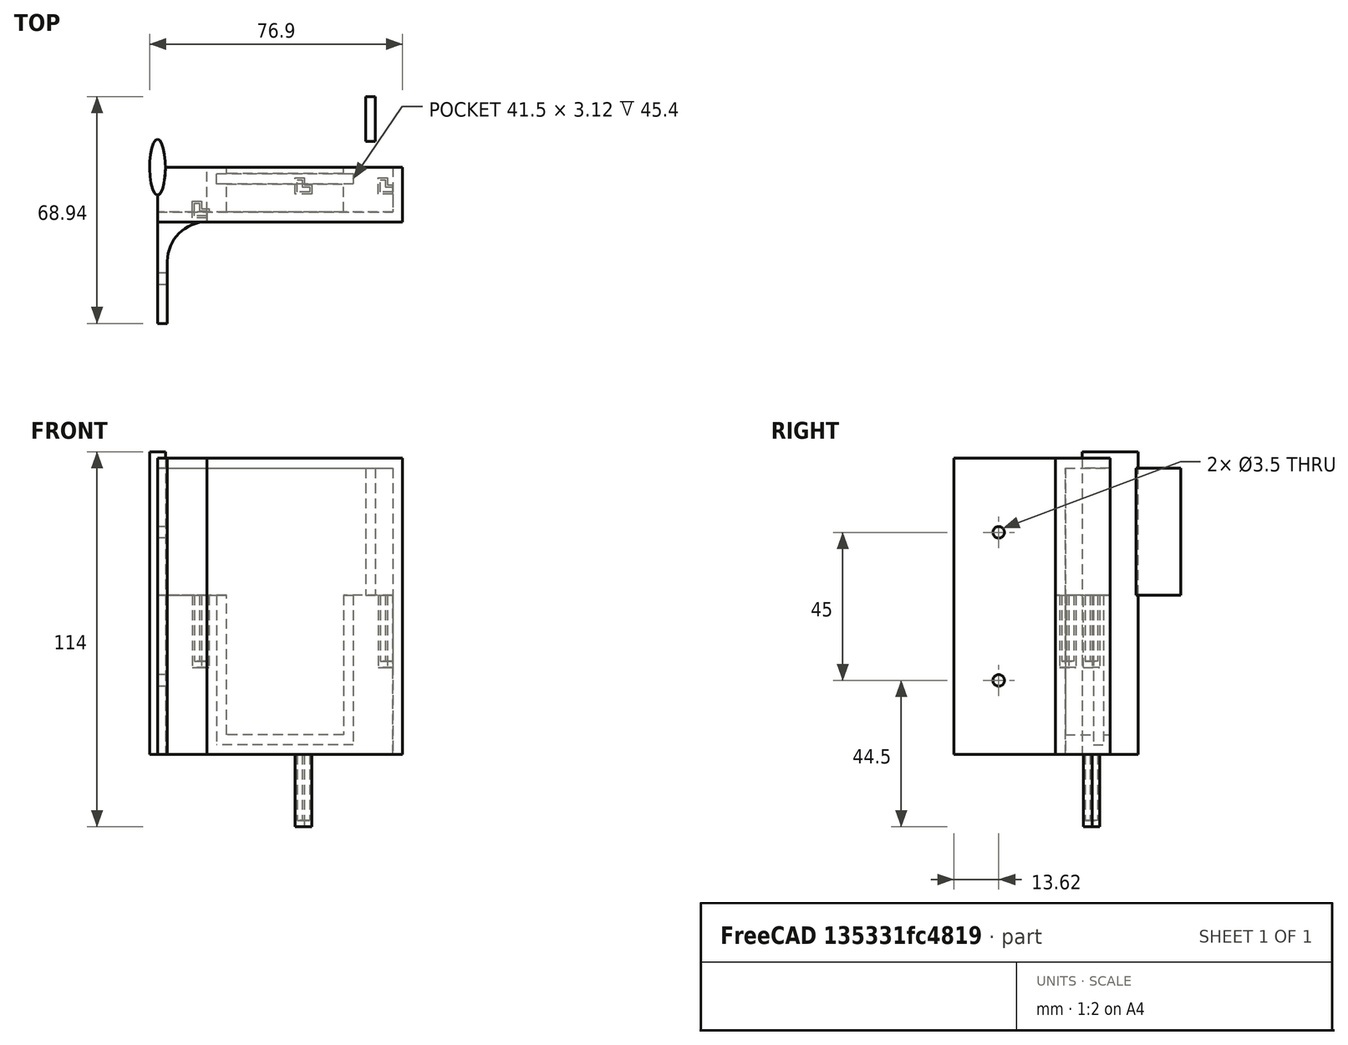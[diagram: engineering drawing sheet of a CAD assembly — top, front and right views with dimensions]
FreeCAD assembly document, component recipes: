
FREECAD ASSEMBLY — COMPONENT RECIPES ("rfid_mk2")

This assembly document has 9 components, labeled P0..P8 below (a component is one placed body or linked part). 8 of them carry a construction recipe — the FreeCAD feature program that regenerates the part from scratch, quoted from this document or its linked companion documents; the rest are supplied as boundary geometry only. No exploded tour is included for this assembly.
COMPONENT P0 — recipe-attached ("Holder", modeled in this document).
Construction recipe (the document's own serialized feature program — sketch geometry with constraints, then the solid features built on it; lengths are millimeters unless a unit is written):

FEATURE [Sketcher::SketchObject] Sketch  label="Holder Sketch"
  FullyConstrained = false
  MapMode = 5
  Support = -> [XY_Plane]
  expr: Constraints[8] = <<Holder Data>>.width
  expr: Constraints[9] = <<Holder Data>>.thick
  sketch-geometry (4):
    g0: LineSegment StartX=-28.25 StartY=6.81 StartZ=0 EndX=28.25 EndY=6.81 EndZ=0
    g1: LineSegment StartX=28.25 StartY=6.81 StartZ=0 EndX=28.25 EndY=-6.81 EndZ=0
    g2: LineSegment StartX=28.25 StartY=-6.81 StartZ=0 EndX=-28.25 EndY=-6.81 EndZ=0
    g3: LineSegment StartX=-28.25 StartY=-6.81 StartZ=0 EndX=-28.25 EndY=6.81 EndZ=0
  constraints (10):
    c: Coincident(g0,g1)
    c: Coincident(g1,g2)
    c: Coincident(g2,g3)
    c: Coincident(g3,g0)
    c: Horizontal(g2)
    c: Vertical(g3)
    c: Symmetric(g0,g0,g-2)
    c: Symmetric(g1,g0,g-1)
    c: DistanceX(g0,g0) = 56.5
    c: DistanceY(g1,g0) = 13.62
FEATURE [PartDesign::Pad] Pad  label="Holder Pad"
  AllowMultiFace = false
  Direction = (1,1,1)
  Length = 48.4
  Length2 = 100
  Profile = -> Sketch
  Type = 0
  expr: Length = <<Holder Data>>.height
FEATURE [Sketcher::SketchObject] Sketch001  label="RFID Slot"
  FullyConstrained = false
  MapMode = 5
  Placement = pos=(0,0,48.4) rot=(0,0,1;0rad)
  Support = -> [Pad]
  expr: Constraints[11] = <<Holder Data>>.thick / 2 - <<Holder Data>>.glass_clearance
  expr: Constraints[2] = <<Holder Data>>.rfid_gap
  expr: Constraints[10] = -<<Holder Data>>.width / 2 + <<General Data>>.wall
  expr: Constraints[1] = <<Holder Data>>.slot
  sketch-geometry (4):
    g0: LineSegment StartX=-25.25 StartY=4.81 StartZ=0 EndX=16.25 EndY=4.81 EndZ=0
    g1: LineSegment StartX=16.25 StartY=4.81 StartZ=0 EndX=16.25 EndY=1.69 EndZ=0
    g2: LineSegment StartX=16.25 StartY=1.69 StartZ=0 EndX=-25.25 EndY=1.69 EndZ=0
    g3: LineSegment StartX=-25.25 StartY=1.69 StartZ=0 EndX=-25.25 EndY=4.81 EndZ=0
  constraints (12):
    c: Vertical(g1)
    c: DistanceY(g1,g1) = 3.12
    c: DistanceX(g0,g0) = 41.5
    c: Coincident(g3,g0)
    c: Coincident(g1,g0)
    c: Coincident(g2,g1)
    c: Horizontal(g0)
    c: Horizontal(g2)
    c: Vertical(g3)
    c: Coincident(g2,g3)
    c: DistanceX(g-1,g2) = -25.25
    c: DistanceY(g-1,g0) = 4.81
FEATURE [PartDesign::Pocket] Pocket  label="RFID Slot Pocket"
  AllowMultiFace = false
  BaseFeature = -> Pad
  Length = 45.4
  Length2 = 100
  Profile = -> Sketch001
  Type = 0
  expr: Length = <<Holder Data>>.height - <<General Data>>.wall
FEATURE [Sketcher::SketchObject] Sketch002  label="Through Holder"
  FullyConstrained = false
  MapMode = 5
  Placement = pos=(0,-6.81,0) rot=(1,0,0;1.5708rad)
  Support = -> [Pocket]
  expr: Constraints[7] = <<General Data>>.wall * 2
  expr: Constraints[8] = <<Holder Data>>.height
  expr: Constraints[9] = <<Holder Data>>.width / 2 - <<General Data>>.wall * 2
  expr: Constraints[10] = <<Holder Data>>.rfid_gap - <<General Data>>.wall * 2
  sketch-geometry (4):
    g0: LineSegment StartX=-22.25 StartY=48.4 StartZ=0 EndX=13.25 EndY=48.4 EndZ=0
    g1: LineSegment StartX=13.25 StartY=48.4 StartZ=0 EndX=13.25 EndY=6 EndZ=0
    g2: LineSegment StartX=13.25 StartY=6 StartZ=0 EndX=-22.25 EndY=6 EndZ=0
    g3: LineSegment StartX=-22.25 StartY=6 StartZ=0 EndX=-22.25 EndY=48.4 EndZ=0
  constraints (11):
    c: Coincident(g0,g1)
    c: Coincident(g1,g2)
    c: Coincident(g2,g3)
    c: Coincident(g3,g0)
    c: Horizontal(g0)
    c: Vertical(g1)
    c: Vertical(g3)
    c: DistanceY(g-1,g2) = 6
    c: DistanceY(g-1,g0) = 48.4
    c: DistanceX(g2,g-1) = 22.25
    c: DistanceX(g2,g2) = 35.5
FEATURE [PartDesign::Pocket] Pocket001  label="Through Holder Pocket"
  AllowMultiFace = false
  BaseFeature = -> Pocket
  Length = 56.5
  Length2 = 100
  Profile = -> Sketch002
  Type = 0
  expr: Length = <<Holder Data>>.width
FEATURE [PartDesign::Body] Body  label="Holder"
  Group = -> [Sketch,Pad,Sketch001,Pocket,Sketch002,Pocket001]
  Origin = -> Origin
  Tip = -> Pocket001
COMPONENT P1 — recipe-attached ("Bracket Base", modeled in this document).
Construction recipe (the document's own serialized feature program — sketch geometry with constraints, then the solid features built on it; lengths are millimeters unless a unit is written):

FEATURE [Sketcher::SketchObject] Sketch003  label="Bracket Sketch"
  FullyConstrained = false
  MapMode = 5
  Support = -> [XY_Plane001]
  expr: Constraints[13] = <<Bracket Data>>.depth
  expr: Constraints[14] = <<General Data>>.wall
  expr: Constraints[15] = <<Bracket Data>>.width
  expr: Constraints[16] = <<Holder Data>>.thick + <<General Data>>.wall
  expr: Constraints[18] = <<Holder Data>>.thick / 2
  expr: Constraints[19] = <<Holder Data>>.width / 2
  expr: Constraints[17] = <<Bracket Data>>.width - <<General Data>>.wall - 0.01
  sketch-geometry (7):
    g0: LineSegment StartX=-43.25 StartY=6.81 StartZ=0 EndX=-43.25 EndY=-40.69 EndZ=0
    g1: LineSegment StartX=-43.25 StartY=-40.69 StartZ=0 EndX=-40.25 EndY=-40.69 EndZ=0
    g2: LineSegment StartX=-40.25 StartY=-40.69 StartZ=0 EndX=-40.25 EndY=-21.8 EndZ=0
    g3: LineSegment StartX=-28.26 StartY=-9.81 StartZ=0 EndX=-28.25 EndY=-9.81 EndZ=0
    g4: LineSegment StartX=-28.25 StartY=-9.81 StartZ=0 EndX=-28.25 EndY=6.81 EndZ=0
    g5: LineSegment StartX=-28.25 StartY=6.81 StartZ=0 EndX=-43.25 EndY=6.81 EndZ=0
    g6: ArcOfCircle CenterX=-28.26 CenterY=-21.8 CenterZ=0 NormalX=0 NormalY=0 NormalZ=1 AngleXU=0 Radius=11.99 StartAngle=1.5708 EndAngle=3.14159
  constraints (20):
    c: Vertical(g0)
    c: Coincident(g0,g1)
    c: Coincident(g1,g2)
    c: Vertical(g2)
    c: Horizontal(g3)
    c: Coincident(g3,g4)
    c: Vertical(g4)
    c: Coincident(g4,g5)
    c: Coincident(g5,g0)
    c: Horizontal(g5)
    c: Horizontal(g1)
    c: Tangent(g2,g6) = 1.5708
    c: Tangent(g3,g6) = 1.5708
    c: DistanceY(g0,g0) = 47.5
    c: DistanceX(g1,g1) = 3
    c: DistanceX(g5,g5) = 15
    c: DistanceY(g4,g4) = 16.62
    c: Radius(g6) = 11.99
    c: DistanceY(g-1,g4) = 6.81
    c: DistanceX(g4,g-1) = 28.25
FEATURE [PartDesign::Pad] Pad001  label="Bracket Pad"
  AllowMultiFace = false
  Direction = (1,1,1)
  Length = 90
  Length2 = 100
  Profile = -> Sketch003
  Type = 0
  expr: Length = <<General Data>>.height
FEATURE [Sketcher::SketchObject] Sketch004  label="Bracket Block Cutout Sketch"
  FullyConstrained = false
  MapMode = 5
  Placement = pos=(0,0,90) rot=(0,0,1;0rad)
  Support = -> [Pad001]
  expr: Constraints[8] = <<Holder Data>>.thick + <<General Data>>.wall
  expr: Constraints[9] = <<Bracket Data>>.width
  expr: Constraints[10] = <<Holder Data>>.thick / 2
  expr: Constraints[11] = <<Holder Data>>.width / 2
  sketch-geometry (4):
    g0: LineSegment StartX=-43.25 StartY=6.81 StartZ=0 EndX=-28.25 EndY=6.81 EndZ=0
    g1: LineSegment StartX=-28.25 StartY=6.81 StartZ=0 EndX=-28.25 EndY=-9.81 EndZ=0
    g2: LineSegment StartX=-28.25 StartY=-9.81 StartZ=0 EndX=-43.25 EndY=-9.81 EndZ=0
    g3: LineSegment StartX=-43.25 StartY=-9.81 StartZ=0 EndX=-43.25 EndY=6.81 EndZ=0
  constraints (12):
    c: Coincident(g0,g1)
    c: Coincident(g1,g2)
    c: Coincident(g2,g3)
    c: Coincident(g3,g0)
    c: Horizontal(g0)
    c: Horizontal(g2)
    c: Vertical(g1)
    c: Vertical(g3)
    c: DistanceY(g1,g1) = 16.62
    c: DistanceX(g0,g0) = 15
    c: DistanceY(g-1,g0) = 6.81
    c: DistanceX(g0,g-1) = 28.25
FEATURE [PartDesign::Pocket] Pocket002  label="Bracket Block Cutout"
  AllowMultiFace = false
  BaseFeature = -> Pad001
  Length = 41.6
  Length2 = 100
  Profile = -> Sketch004
  Type = 0
  expr: Length = <<General Data>>.height - <<Holder Data>>.height
FEATURE [PartDesign::Boolean] Boolean  label="Union with Holder"
  BaseFeature = -> Pocket002
  Group = -> [Body]
  Type = 0
FEATURE [Sketcher::SketchObject] Sketch012  label="Rivit Holes"
  FullyConstrained = false
  MapMode = 5
  Placement = pos=(-43.25,0,0) rot=(0.57735,-0.57735,-0.57735;2.0944rad)
  Support = -> [Boolean]
  expr: Constraints[5] = -<<Holder Data>>.thick / 2 + <<Bracket Data>>.depth - <<Holder Data>>.thick
  expr: Constraints[3] = <<General Data>>.height * 3 / 4
  expr: Constraints[2] = <<General Data>>.height * 1 / 4
  expr: Constraints[0] = <<Bracket Data>>.rivit / 2
  sketch-geometry (2):
    g0: Circle CenterX=27.07 CenterY=67.5 CenterZ=0 NormalX=0 NormalY=0 NormalZ=1 AngleXU=0 Radius=1.75
    g1: Circle CenterX=27.07 CenterY=22.5 CenterZ=0 NormalX=0 NormalY=0 NormalZ=1 AngleXU=0 Radius=1.75
  constraints (6):
    c: Radius(g0) = 1.75
    c: Equal(g0,g1)
    c: DistanceY(g-1,g1) = 22.5
    c: DistanceY(g-1,g0) = 67.5
    c: Vertical(g1,g0)
    c: DistanceX(g-1,g1) = 27.07
FEATURE [PartDesign::Pocket] Pocket004
  AllowMultiFace = false
  BaseFeature = -> Boolean
  Length = 3
  Length2 = 100
  Profile = -> Sketch012
  Type = 0
  expr: Length = <<General Data>>.wall
FEATURE [PartDesign::Body] Body001  label="Bracket Base"
  Group = -> [Sketch003,Pad001,Sketch004,Pocket002,Boolean,Sketch012,Pocket004]
  Origin = -> Origin001
  Tip = -> Pocket004
COMPONENT P2 — recipe-attached ("Cover Upper Wall", modeled in this document).
Construction recipe (the document's own serialized feature program — sketch geometry with constraints, then the solid features built on it; lengths are millimeters unless a unit is written):

FEATURE [Sketcher::SketchObject] Sketch013
  FullyConstrained = false
  MapMode = 5
  Placement = pos=(0,0,0) rot=(0.57735,0.57735,0.57735;2.0944rad)
  Support = -> [YZ_Plane007]
  expr: Constraints[8] = <<Holder Data>>.thick
  expr: Constraints[9] = <<General Data>>.height - <<General Data>>.wall - <<Holder Data>>.height
  expr: Constraints[10] = <<General Data>>.height - <<General Data>>.wall
  expr: Constraints[11] = <<Holder Data>>.thick
  sketch-geometry (4):
    g0: LineSegment StartX=-13.62 StartY=87 StartZ=0 EndX=0 EndY=87 EndZ=0
    g1: LineSegment StartX=0 StartY=87 StartZ=0 EndX=0 EndY=48.4 EndZ=0
    g2: LineSegment StartX=0 StartY=48.4 StartZ=0 EndX=-13.62 EndY=48.4 EndZ=0
    g3: LineSegment StartX=-13.62 StartY=48.4 StartZ=0 EndX=-13.62 EndY=87 EndZ=0
  constraints (12):
    c: Coincident(g0,g1)
    c: Coincident(g1,g2)
    c: Coincident(g2,g3)
    c: Coincident(g3,g0)
    c: Horizontal(g0)
    c: Horizontal(g2)
    c: Vertical(g1)
    c: Vertical(g3)
    c: DistanceX(g0,g0) = 13.62
    c: DistanceY(g1,g1) = 38.6
    c: DistanceY(g-1,g0) = 87
    c: DistanceX(g2,g-1) = 13.62
FEATURE [PartDesign::Pad] Pad008
  AllowMultiFace = false
  Direction = (1,1,1)
  Length = 3
  Length2 = 100
  Placement = pos=(0,0,0) rot=(0.57735,0.57735,0.57735;2.0944rad)
  Profile = -> Sketch013
  Type = 0
  expr: Length = <<General Data>>.wall
FEATURE [PartDesign::Body] Body007  label="Cover Upper Wall"
  Group = -> [Sketch013,Pad008]
  Origin = -> Origin007
  Placement = pos=(20,28.25,0) rot=(0,0,1;0rad)
  Tip = -> Pad008
COMPONENT P3 — recipe-attached ("Cover Base001", modeled in this document).
Construction recipe (the document's own serialized feature program — sketch geometry with constraints, then the solid features built on it; lengths are millimeters unless a unit is written):

FEATURE [Sketcher::SketchObject] Sketch005  label="Cover Box Sketch"
  FullyConstrained = false
  MapMode = 5
  Support = -> [XY_Plane002]
  expr: Constraints[8] = <<Holder Data>>.width / 2 + <<General Data>>.wall
  expr: Constraints[9] = <<Holder Data>>.width + <<Bracket Data>>.width + <<General Data>>.wall
  expr: Constraints[10] = <<Holder Data>>.thick / 2
  expr: Constraints[11] = <<Holder Data>>.thick + <<General Data>>.wall
  sketch-geometry (4):
    g0: LineSegment StartX=-43.25 StartY=6.81 StartZ=0 EndX=31.25 EndY=6.81 EndZ=0
    g1: LineSegment StartX=31.25 StartY=6.81 StartZ=0 EndX=31.25 EndY=-9.81 EndZ=0
    g2: LineSegment StartX=31.25 StartY=-9.81 StartZ=0 EndX=-43.25 EndY=-9.81 EndZ=0
    g3: LineSegment StartX=-43.25 StartY=-9.81 StartZ=0 EndX=-43.25 EndY=6.81 EndZ=0
  constraints (12):
    c: Coincident(g0,g1)
    c: Coincident(g1,g2)
    c: Coincident(g2,g3)
    c: Coincident(g3,g0)
    c: Horizontal(g0)
    c: Horizontal(g2)
    c: Vertical(g1)
    c: Vertical(g3)
    c: DistanceX(g-1,g0) = 31.25
    c: DistanceX(g0,g0) = 74.5
    c: DistanceY(g-1,g0) = 6.81
    c: DistanceY(g1,g1) = 16.62
FEATURE [PartDesign::Pad] Pad002  label="Cover Box"
  AllowMultiFace = false
  Direction = (1,1,1)
  Length = 90
  Length2 = 100
  Profile = -> Sketch005
  Type = 0
  expr: Length = <<General Data>>.height
FEATURE [PartDesign::Thickness] Thickness
  Base = -> Pad002 [Face1,Face4,Face5]
  BaseFeature = -> Pad002
  Intersection = false
  Join = 0
  Mode = 0
  Refine = true
  Reversed = true
  SupportTransform = false
  Value = 3
  expr: Value = <<General Data>>.wall
FEATURE [Sketcher::SketchObject] Sketch006  label="Cover Bottom Cutout Sketch"
  FullyConstrained = false
  MapMode = 5
  Placement = pos=(0,0,0) rot=(1,0,0;3.14159rad)
  Support = -> [Thickness]
  expr: Constraints[8] = <<Bracket Data>>.width
  expr: Constraints[9] = <<General Data>>.wall
  expr: Constraints[10] = <<Holder Data>>.thick / 2
  expr: Constraints[11] = <<Holder Data>>.width / 2
  sketch-geometry (4):
    g0: LineSegment StartX=-43.25 StartY=9.81 StartZ=0 EndX=-28.25 EndY=9.81 EndZ=0
    g1: LineSegment StartX=-28.25 StartY=9.81 StartZ=0 EndX=-28.25 EndY=6.81 EndZ=0
    g2: LineSegment StartX=-28.25 StartY=6.81 StartZ=0 EndX=-43.25 EndY=6.81 EndZ=0
    g3: LineSegment StartX=-43.25 StartY=6.81 StartZ=0 EndX=-43.25 EndY=9.81 EndZ=0
  constraints (12):
    c: Coincident(g0,g1)
    c: Coincident(g1,g2)
    c: Coincident(g2,g3)
    c: Coincident(g3,g0)
    c: Horizontal(g0)
    c: Horizontal(g2)
    c: Vertical(g1)
    c: Vertical(g3)
    c: DistanceX(g0,g0) = 15
    c: DistanceY(g3,g3) = 3
    c: DistanceY(g-1,g1) = 6.81
    c: DistanceX(g1,g-1) = 28.25
FEATURE [PartDesign::Pocket] Pocket003  label="Cover Bottom Cutout"
  AllowMultiFace = false
  BaseFeature = -> Thickness
  Length = 48.4
  Length2 = 100
  Profile = -> Sketch006
  Type = 0
  expr: Length = <<Holder Data>>.height
FEATURE [PartDesign::Body] Body002  label="Cover Base"
  Group = -> [Sketch005,Pad002,Thickness,Sketch006,Pocket003]
  Origin = -> Origin002
  Tip = -> Pocket003
COMPONENT P4 — recipe-attached ("Corner Original001", modeled in this document).
Construction recipe (the document's own serialized feature program — sketch geometry with constraints, then the solid features built on it; lengths are millimeters unless a unit is written):

FEATURE [Sketcher::SketchObject] Sketch007  label="Corner Sketch"
  FullyConstrained = false
  MapMode = 5
  Support = -> [XY_Plane003]
  expr: Constraints[5] = <<Holder Data>>.thick / 2
  expr: Constraints[6] = <<Holder Data>>.width / 2 + <<Bracket Data>>.width
  expr: Constraints[7] = <<General Data>>.corner_a * 2
  expr: Constraints[8] = <<General Data>>.corner_b * 2
  sketch-geometry (5):
    g0: Ellipse CenterX=-43.25 CenterY=6.81 CenterZ=0 NormalX=0 NormalY=0 NormalZ=1 MajorRadius=8.5 MinorRadius=2.4 AngleXU=1.5708
    g1: LineSegment StartX=-43.25 StartY=15.31 StartZ=0 EndX=-43.25 EndY=-1.69 EndZ=0
    g2: LineSegment StartX=-45.65 StartY=6.81 StartZ=0 EndX=-40.85 EndY=6.81 EndZ=0
    g3: GeomPoint X=-43.25 Y=14.9641 Z=0
    g4: GeomPoint X=-43.25 Y=-1.34414 Z=0
  constraints (6):
    c: InternalAlignment(g1-g4 -> g0) x4
    c: Horizontal(g2)
    c: DistanceY(g-1,g0) = 6.81
    c: DistanceX(g0,g-1) = 43.25
    c: DistanceY(g1,g1) = 17
    c: DistanceX(g2,g2) = 4.8
FEATURE [PartDesign::Pad] Pad003
  AllowMultiFace = false
  Direction = (1,1,1)
  Length = 92
  Length2 = 100
  Profile = -> Sketch007
  Type = 0
  expr: Length = <<General Data>>.height + 2
FEATURE [PartDesign::Body] Body003  label="Corner Original"
  Group = -> [Sketch007,Pad003]
  Origin = -> Origin003
  Tip = -> Pad003
COMPONENT P5 — same part as P4; its construction recipe is shown at P4.
COMPONENT P6 — recipe-attached ("Rail Left", modeled in this document).
Construction recipe (the document's own serialized feature program — sketch geometry with constraints, then the solid features built on it; lengths are millimeters unless a unit is written):

FEATURE [Sketcher::SketchObject] Sketch010  label="Rail Sketch"
  FullyConstrained = false
  MapMode = 5
  Support = -> [XY_Plane005]
  expr: Constraints[12] = <<General Data>>.rail_thick
  expr: Constraints[13] = <<General Data>>.rail_thick
  expr: Constraints[14] = <<General Data>>.rail_size
  expr: Constraints[15] = <<General Data>>.rail_size
  sketch-geometry (6):
    g0: LineSegment StartX=3 StartY=-0.75 StartZ=0 EndX=-0.75 EndY=-0.75 EndZ=0
    g1: LineSegment StartX=-0.75 StartY=-0.75 StartZ=0 EndX=-0.75 EndY=3 EndZ=0
    g2: LineSegment StartX=-0.75 StartY=3 StartZ=0 EndX=0.75 EndY=3 EndZ=0
    g3: LineSegment StartX=0.75 StartY=3 StartZ=0 EndX=0.75 EndY=0.75 EndZ=0
    g4: LineSegment StartX=0.75 StartY=0.75 StartZ=0 EndX=3 EndY=0.75 EndZ=0
    g5: LineSegment StartX=3 StartY=0.75 StartZ=0 EndX=3 EndY=-0.75 EndZ=0
  constraints (16):
    c: Horizontal(g0)
    c: Coincident(g0,g1)
    c: Vertical(g1)
    c: Coincident(g1,g2)
    c: Coincident(g2,g3)
    c: Vertical(g3)
    c: Coincident(g3,g4)
    c: Horizontal(g4)
    c: Coincident(g4,g5)
    c: Coincident(g5,g0)
    c: Symmetric(g1,g2,g-2)
    c: Symmetric(g0,g4,g-1)
    c: DistanceX(g2,g2) = 1.5
    c: DistanceY(g5,g5) = 1.5
    c: DistanceX(g-1,g0) = 3
    c: DistanceY(g-1,g1) = 3
FEATURE [PartDesign::Pad] Pad006  label="Rail Pad"
  AllowMultiFace = false
  Direction = (1,1,1)
  Length = 20
  Length2 = 100
  Profile = -> Sketch010
  Reversed = true
  Type = 0
  expr: Length = <<General Data>>.rail_height
FEATURE [PartDesign::Body] Body005  label="Rail Body Original"
  Group = -> [Sketch010,Pad006]
  Origin = -> Origin005
  Tip = -> Pad006
COMPONENT P7 — same part as P6; its construction recipe is shown at P6.
COMPONENT P8 — geometry summary ("Rail Cutout Right"; no construction recipe available for this part):
  bounding box: 22.0 x 5.0 x 5.0 mm
  tessellated surface: 20 triangles
  volume: 439 mm^3 (80% of its bounding box)
  symmetry: mirror-symmetric across its z mid-plane
PROVENANCE & LICENSES
A FreeCAD (.FCStd) document from a public repository crawl; recipes are the document's own serialized feature recipes (and, for linked parts, companion documents' recipes).
License: as declared in the source repository (recorded in the dataset sidecar).
